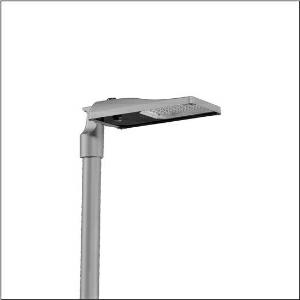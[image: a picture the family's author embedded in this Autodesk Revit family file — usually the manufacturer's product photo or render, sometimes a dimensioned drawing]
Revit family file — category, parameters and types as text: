
# Revit family: streetlight_sl_31_mini___p0_8a_5xh2u4at08ja_add1
name_source: partatom
category: Lighting Fixtures
units: mm (PartAtom-declared; Revit-internal decimal feet)

## family parameters
Cut with Voids When Loaded = No
Host = Face
Light Source = No
Part Type = Normal
Room Calculation Point = No
Round Connector Dimension = Use Diameter
Shared = No

## types (1)
- --- (1 x LED, 12820 lm, 82.5 W, 4000K)
    Apparent Load = 83 VA
    CIE Flux Codes = 36 69 97 100 100
    Color Rendering = 70
    Color Temperature = 4000K
    Default Elevation = 1800 mm
    Description = Streetlight SL 31 mini D4i mast luminaire for post-top, side-entry; light control with lens of PMMA; light distribution: P0.8a, direct asymmetric distribution, for standard-compliant lighting for roads and squares; LED: luminous flux: 12.820lm, light colour: 740, colour temperature: 4000K; luminous efficacy: 155,4lm/W; control: pre-setting: logarithmic dimming characteristic, flexible luminous flux parameterisation, time-dependent luminous flux control, constant luminous flux control, power reduction, intelligent temperature release in ECG and LED module, overheat protection; luminaire housing, of diecast aluminium, Siteco® metallic grey (DB 702S), corrosivity category C5 high according to DIN EN ISO 12944; cover of toughened safety glass, transparent, mast flange of diecast aluminium, Siteco® metallic grey (DB 702S), spigot size: 76/60mm, mast flange included unmounted; with cable H07RN-F 2x 1.5mm², cable length: 10,5m, connection cable pre-assembled; mains connection: 220..240V, AC, 50/60Hz; power consumption (at start of service life): 82,5W / (at end of service life): 90,1W / (with reduced operation 50%): 36,8W; protection rating (complete): IP66; insulation class (complete): insulation class II (safety insulation); impact resistance: IK09; certification: CE, ENEC, ENEC+, VDE, UKCA, ZD4i; permissible operating ambient temperature for outdoor applications: -40..+50°C; packaging unit: 1 piece

Light Distribution: P0.8a
    Height = 76 mm
    Lamp = 1 x LED
    Lamp Light Flux = 12820 lm
    Lamp Power = 82.5 W
    Lamp count = 1
    Length = 547 mm
    Luminous efficacy = 155 lm/W
    Manufacturer = Siteco
    ModVariant = No
    Model = 5XH2U4AT08JA
    Number of Poles = 1
    OnlyDefault = Yes
    Power Factor = 1
    Product Name = Streetlight SL 31 mini | P0.8a
    Product group = mast luminaire | pylon top
    ProductGroupID = 6100
    Protection Class = Protection class II
    Protection Degree = IP 66
    RLX_Detail_Level = 1
    RLX_Emergency_Light_Flux = 0 lm
    RLX_Emergency_Type = 0
    RLX_Emergency_Type_DB = No
    RlxData = <blob elided: 39681 chars, md5=2d2bacbe>
    Socket = socket
    Standby Power = 0 W
    System Light Flux = 12820 lm
    System Power = 83 W
    Type Comments = factory setting: luminous flux: 100 % | dim-lin: 254 | 870 mA
    Type Image = l_1300332.jpg
    URL = http://relux.com
    VarID = @adj_058752
    Voltage = 0 V
    Weight = 0.00 kg
    Width = 265 mm

## geometry (parser evidence)
native form markers: Blend x4, Sweep x9
no freeform markers — native parametric forms only
